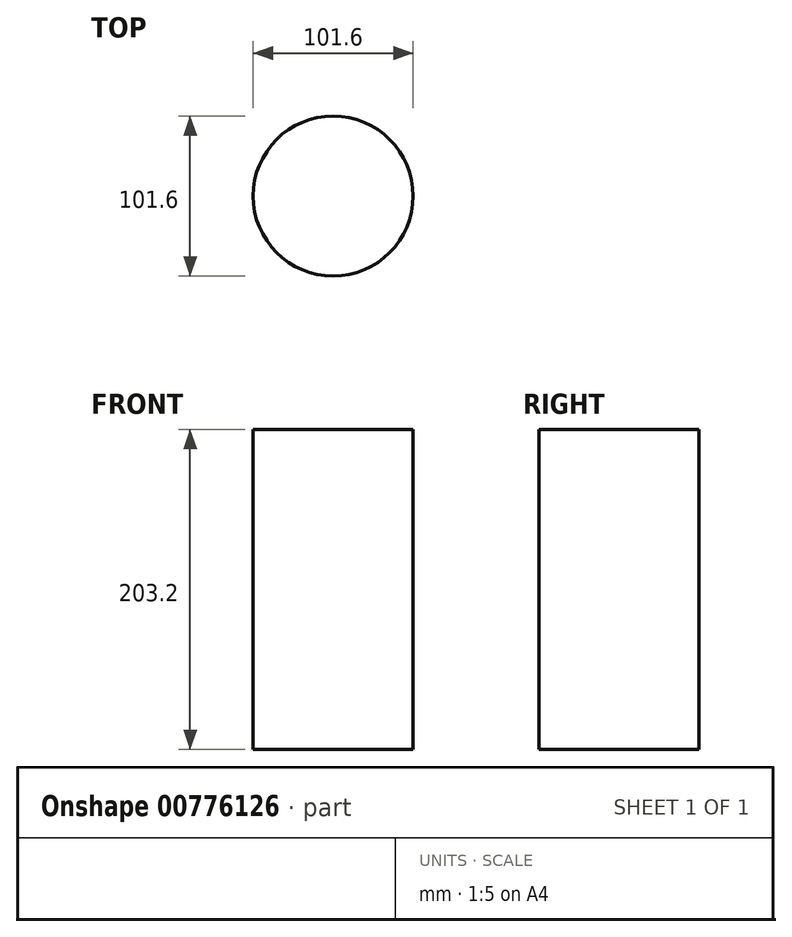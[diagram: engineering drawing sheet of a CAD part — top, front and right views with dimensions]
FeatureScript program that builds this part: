
annotation { "Feature Type Name" : "Feature", "Feature Type Description" : "" }
export const myFeature = defineFeature(function(context is Context, id is Id, definition is map)
    precondition{}
    {
        {
            var Q0;
            Q0=qCreatedBy(makeId("Front.planeOp"),FACE);
            var sketch = newSketch(context, id + "F0", { "sketchPlane" : qUnion([Q0])});
            skLineSegment(sketch, "E0", {"start": v(0, 0) * mm, "end": v(0, 114.5) * mm});
            skSolve(sketch);
        }
        {
            var Q0;
            Q0=qCreatedBy(makeId("Front.planeOp"),FACE);
            var sketch = newSketch(context, id + "F1", { "sketchPlane" : qUnion([Q0])});
            skLineSegment(sketch, "E1", {"start": v(50.8, 203.2) * mm, "end": v(50.8, 0) * mm});
            skLineSegment(sketch, "E2", {"start": v(50.8, 0) * mm, "end": v(13.38, 0) * mm});
            skSolve(sketch);
        }
        {
            var Q0;
            Q0 = qSketchRegion(id + "F1", true);
            var Q1;
            Q1=sQuery(id+"F1.wireOp",EDGE,"E1");
            var Q2;
            Q2=sQuery(id+"F0.wireOp",EDGE,"E0");
            revolve(context, id + "F2", {"bodyType" : ToolBodyType.SURFACE, "surfaceOperationType" : NewSurfaceOperationType.NEW, "entities" : qUnion([Q0]), "surfaceEntities" : qUnion([Q1]), "axis" : qUnion([Q2]), "revolveType" : RevolveType.FULL});
        }
    });
